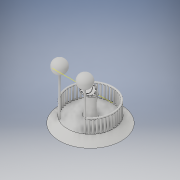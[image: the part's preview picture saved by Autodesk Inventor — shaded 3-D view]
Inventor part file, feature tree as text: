
AUTODESK INVENTOR PART (.ipt)
format: ipt  version: 2017 (Build 210142000, 142)  size: 1,376,256 bytes
history: native  units: in
note: dims shown in document units (in); Inventor stores cm internally (conversion verified against a paired STEP export)
features: other x23, loft x16, sketch x13, extrude x7, plane x1, fillet x1
ambient origin geometry x8: Origin, YZ Plane, XZ Plane, XY Plane, X Axis, Y Axis, Z Axis, Center Point
bodies: Body1 (feature_tree), Body2 (feature_tree)
feature tree (61):
  other  "bace + terminal"
  other  "bace of terminal"
  other  "middle workplane"
  other  "middle"
  other  "top workplane"
  loft  "curved tower"
  other  "pivit point for face of terminal"
  other  "Work Axis1"
  other  "terminal curve"
  other  "face of terminal"
  loft  "terminal face out"
  sketch  "Sketch10"  dims[d2=2.0in d3=0.8in]
  plane  "Work Plane7"
  sketch  "Sketch11"  dims[d4=0.55in d5=1.0in]
  loft  "terminal hole 1"
  loft  "terminal hole 2"
  loft  "terminal hole 3"
  loft  "terminal hole 4"
  loft  "terminal hole 5"
  loft  "terminal hole 6"
  loft  "terminal hole 7"
  loft  "terminal hole 8"
  loft  "terminal hole 9"
  loft  "terminal hole 10"
  loft  "terminal hole 11"
  loft  "terminal hole 12"
  loft  "terminal hole 13"
  loft  "terminal hole 14"
  fillet  "cuved edjes on termanal face"  [1 undecoded]
  extrude  "back hole for button"  TaperAngle=0.0deg  [1 undecoded]
  extrude  "side gap"  TaperAngle=0.0deg  [1 undecoded]
  extrude  "button"  TaperAngle=0.0deg  [1 undecoded]
  extrude  "bace"  TaperAngle=0.0deg  [1 undecoded]
  other  "ramp around"
  extrude  "railing bars"  TaperAngle=0.0deg  [1 undecoded]
  other  "railing bar top workplane"
  other  "railing bar top"
  extrude  "light pole"  TaperAngle=0.0deg  [1 undecoded]
  other  "globe light workplane"
  sketch  "Sketch20"  dims[d39=-0.2in]
  other  "light 1"
  other  "light 2"
  other  "Work Axis7"
  extrude  "Extrusion7"  TaperAngle=0.0deg  [1 undecoded]
  other  "top"
  sketch  "Sketch8"  dims[d0=1.0in d1=0.75in]
  other  "Edges1"
  sketch  "Sketch12"  dims[d6=0.75in d7=1.0in]
  sketch  "Sketch13"  dims[d8=0.0in d9=90.0deg d10=0.0in d11=90.0deg d12=0.0in d13=90.0deg d16=45.0deg]
  sketch  "Sketch14"  dims[d18=0.2in d19=1.2in]
  other  "terminal button"
  sketch  "Sketch15"  dims[d20=0.85in d21=0.0in d22=90.0deg]
  sketch  "Sketch16"  dims[d23=0.0in d24=90.0deg d27=1.1in]
  sketch  "Sketch17"  dims[d28=0.75in d29=1.0in]
  other  "Work Axis3"
  other  "Work Axis4"
  sketch  "Sketch18"  dims[d30=0.65in d33=0.0481in]
  sketch  "Sketch19"  dims[d34=0.0481in d35=5.5118in d37=360.0deg]
  other  "Work Axis5"
  other  "Work Axis6"
  sketch  "Sketch21"  dims[d41=5.5118in d42=1.1in d43=0.85in d44=1.0in d45=0.75in d46=0.0481in d47=0.0481in d48=360.0deg d49=1.2in d50=0.85in d51=1.0in d52=0.75in d53=0.0in d54=90.0deg d55=0.0in d56=90.0deg d57=0.0in d58=90.0deg d59=0.0in d60=90.0deg d61=0.0in d62=90.0deg d63=0.0in d64=90.0deg d65=0.0in d66=90.0deg d67=0.0in d68=90.0deg d69=0.0in d70=90.0deg d71=0.0in d72=90.0deg d73=0.0in d74=90.0deg d75=0.0in d76=90.0deg d77=0.0in d78=90.0deg d79=0.0in d80=90.0deg d81=0.0in d82=90.0deg d83=0.0in d84=90.0deg d85=0.0in d86=90.0deg d87=0.0in d88=90.0deg d89=0.0in d90=90.0deg d91=0.0in d92=90.0deg d93=0.0in d94=90.0deg d95=0.0in d96=90.0deg d97=0.0in d98=90.0deg d99=0.0in d100=90.0deg d105=0.0in d106=90.0deg d107=0.0in d108=90.0deg d109=0.0in d110=90.0deg d111=0.0in d112=90.0deg d113=0.01in d114=1.0in d115=0.1in d116=0.0in d117=1.1in d118=0.05in d119=0.0in d120=0.05in d121=0.0in d122=7.0in d123=1.0in d124=0.0in d134=0.7579in d135=15.748in d137=1.9948in d139=2.0in d140=0.0in d141=0.2749in d142=90.0deg d143=0.25in d144=0.25in d145=90.0deg d146=4.0in d147=0.0in d150=2.0in d151=0.9in d152=2.0in d153=0.9in d155=90.0deg d156=90.0deg d157=1.0in d158=2.0in d159=0.2in d160=0.0in]
note: 8 required parameter values undecoded (feature->parameter linkage not recoverable at this tier; creation-order binding heuristic only, values carry confidence <= 0.55)
